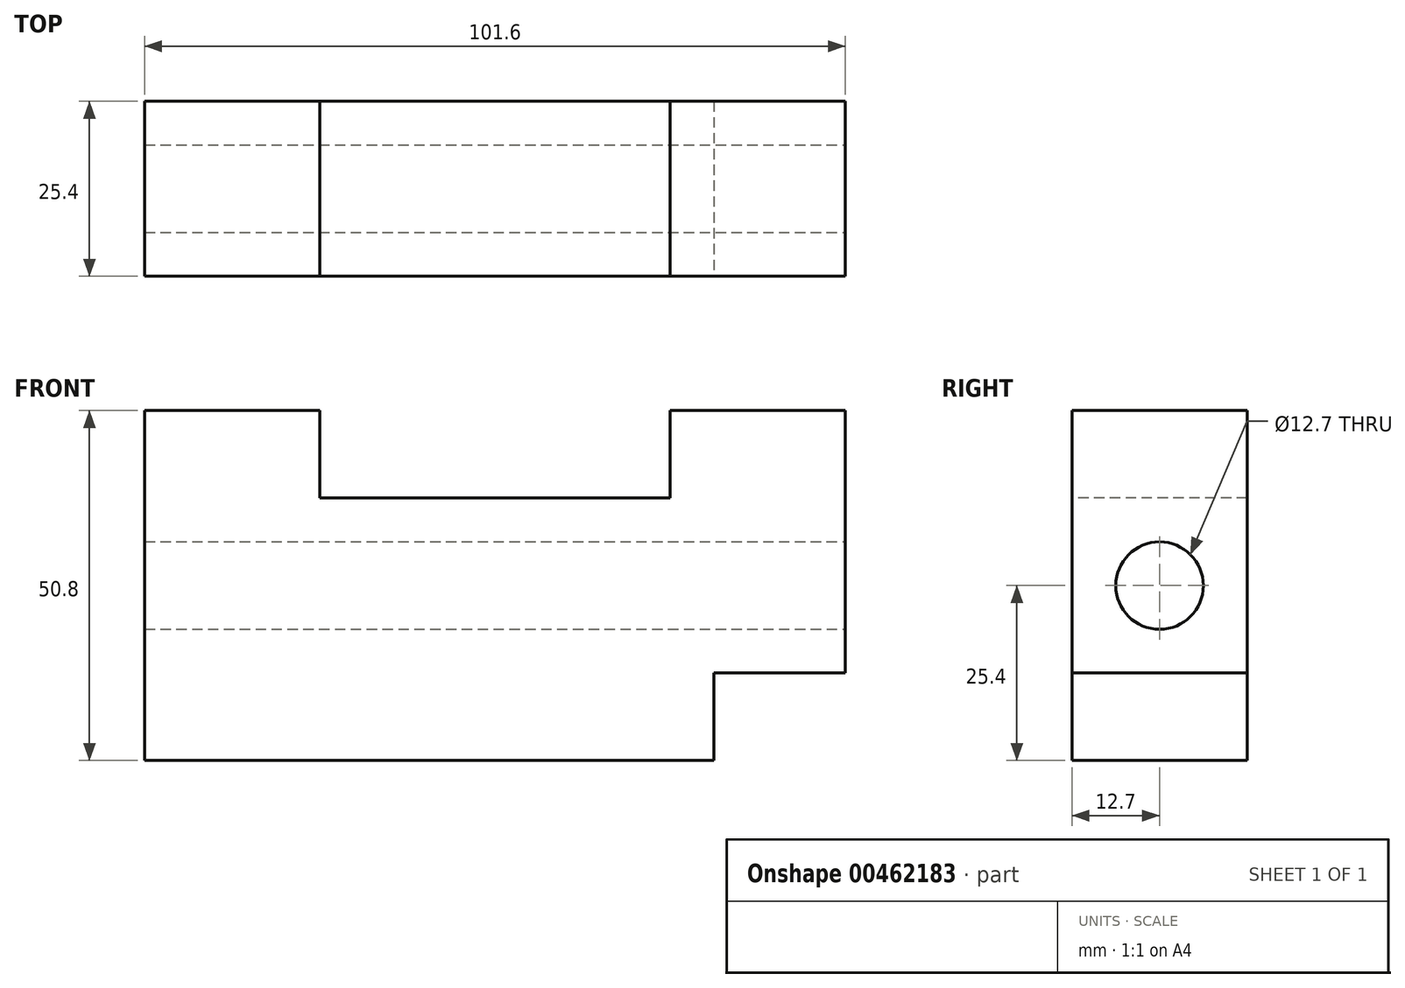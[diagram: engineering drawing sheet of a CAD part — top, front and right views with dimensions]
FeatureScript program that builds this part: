
annotation { "Feature Type Name" : "Feature", "Feature Type Description" : "" }
export const myFeature = defineFeature(function(context is Context, id is Id, definition is map)
    precondition{}
    {
        {
            var Q0;
            Q0=qCreatedBy(makeId("Front.planeOp"),FACE);
            var sketch = newSketch(context, id + "F0", { "sketchPlane" : qUnion([Q0])});
            skLineSegment(sketch, "E0.bottom", {"start": v(50.8, -25.4) * mm, "end": v(-50.8, -25.4) * mm});
            skLineSegment(sketch, "E0.top", {"start": v(50.8, 25.4) * mm, "end": v(-50.8, 25.4) * mm});
            skLineSegment(sketch, "E0.left", {"start": v(50.8, -25.4) * mm, "end": v(50.8, 25.4) * mm});
            skLineSegment(sketch, "E0.right", {"start": v(-50.8, -25.4) * mm, "end": v(-50.8, 25.4) * mm});
            skPoint(sketch, "E0.middle", {"position": v(0, 0) * mm});
            skSolve(sketch);
        }
        {
            var Q0;
            Q0 = qSketchRegion(id + "F0", true);
            extrude(context, id + "F1", {"entities" : qUnion([Q0]), "depth" : 25.4 * mm});
        }
        {
            var Q0;
            Q0=makeQuery(id+"F1.opExtrude","CAP_FACE",FACE,{"disambiguationData":[OSD([sQuery(id+"F0.wireOp",EDGE,"E0.bottom"),sQuery(id+"F0.wireOp",EDGE,"E0.top"),sQuery(id+"F0.wireOp",EDGE,"E0.left"),sQuery(id+"F0.wireOp",EDGE,"E0.right")])],"isStart":false});
            var sketch = newSketch(context, id + "F2", { "sketchPlane" : qUnion([Q0])});
            skLineSegment(sketch, "E1.bottom", {"start": v(50.8, -25.4) * mm, "end": v(31.75, -25.4) * mm});
            skLineSegment(sketch, "E1.top", {"start": v(50.8, -12.7) * mm, "end": v(31.75, -12.7) * mm});
            skLineSegment(sketch, "E1.left", {"start": v(50.8, -25.4) * mm, "end": v(50.8, -12.7) * mm});
            skLineSegment(sketch, "E1.right", {"start": v(31.75, -25.4) * mm, "end": v(31.75, -12.7) * mm});
            skSolve(sketch);
        }
        {
            var Q0;
            Q0 = qSketchRegion(id + "F2", true);
            extrude(context, id + "F3", {"entities" : qUnion([Q0]), "operationType" : NewBodyOperationType.REMOVE, "oppositeDirection" : true, "depth" : 25.4 * mm});
        }
        {
            var Q0;
            Q0=makeQuery(id+"F1.opExtrude","CAP_FACE",FACE,{"disambiguationData":[OSD([sQuery(id+"F0.wireOp",EDGE,"E0.bottom"),sQuery(id+"F0.wireOp",EDGE,"E0.top"),sQuery(id+"F0.wireOp",EDGE,"E0.left"),sQuery(id+"F0.wireOp",EDGE,"E0.right")])],"isStart":false});
            var sketch = newSketch(context, id + "F4", { "sketchPlane" : qUnion([Q0])});
            skLineSegment(sketch, "E2.bottom", {"start": v(-25.4, 12.7) * mm, "end": v(25.4, 12.7) * mm});
            skLineSegment(sketch, "E2.top", {"start": v(-25.4, 38.1) * mm, "end": v(25.4, 38.1) * mm});
            skLineSegment(sketch, "E2.left", {"start": v(-25.4, 12.7) * mm, "end": v(-25.4, 38.1) * mm});
            skLineSegment(sketch, "E2.right", {"start": v(25.4, 12.7) * mm, "end": v(25.4, 38.1) * mm});
            skPoint(sketch, "E2.middle", {"position": v(0, 25.4) * mm});
            skSolve(sketch);
        }
        {
            var Q0;
            Q0 = qSketchRegion(id + "F4", true);
            extrude(context, id + "F5", {"entities" : qUnion([Q0]), "operationType" : NewBodyOperationType.REMOVE, "oppositeDirection" : true, "depth" : 25.4 * mm});
        }
        {
            var Q0;
            Q0=makeQuery(id+"F1.opExtrude","SWEPT_FACE",FACE,{"disambiguationData":[OSD([sQuery(id+"F0.wireOp",EDGE,"E0.left")])]});
            var sketch = newSketch(context, id + "F6", { "sketchPlane" : qUnion([Q0])});
            skCircle(sketch, "E3", {"center": v(-12.7, 0) * mm, "radius": 6.35 * mm});
            skSolve(sketch);
        }
        {
            var Q0;
            Q0 = qSketchRegion(id + "F6", true);
            extrude(context, id + "F7", {"entities" : qUnion([Q0]), "operationType" : NewBodyOperationType.REMOVE, "oppositeDirection" : true, "depth" : 101.6 * mm});
        }
    });
